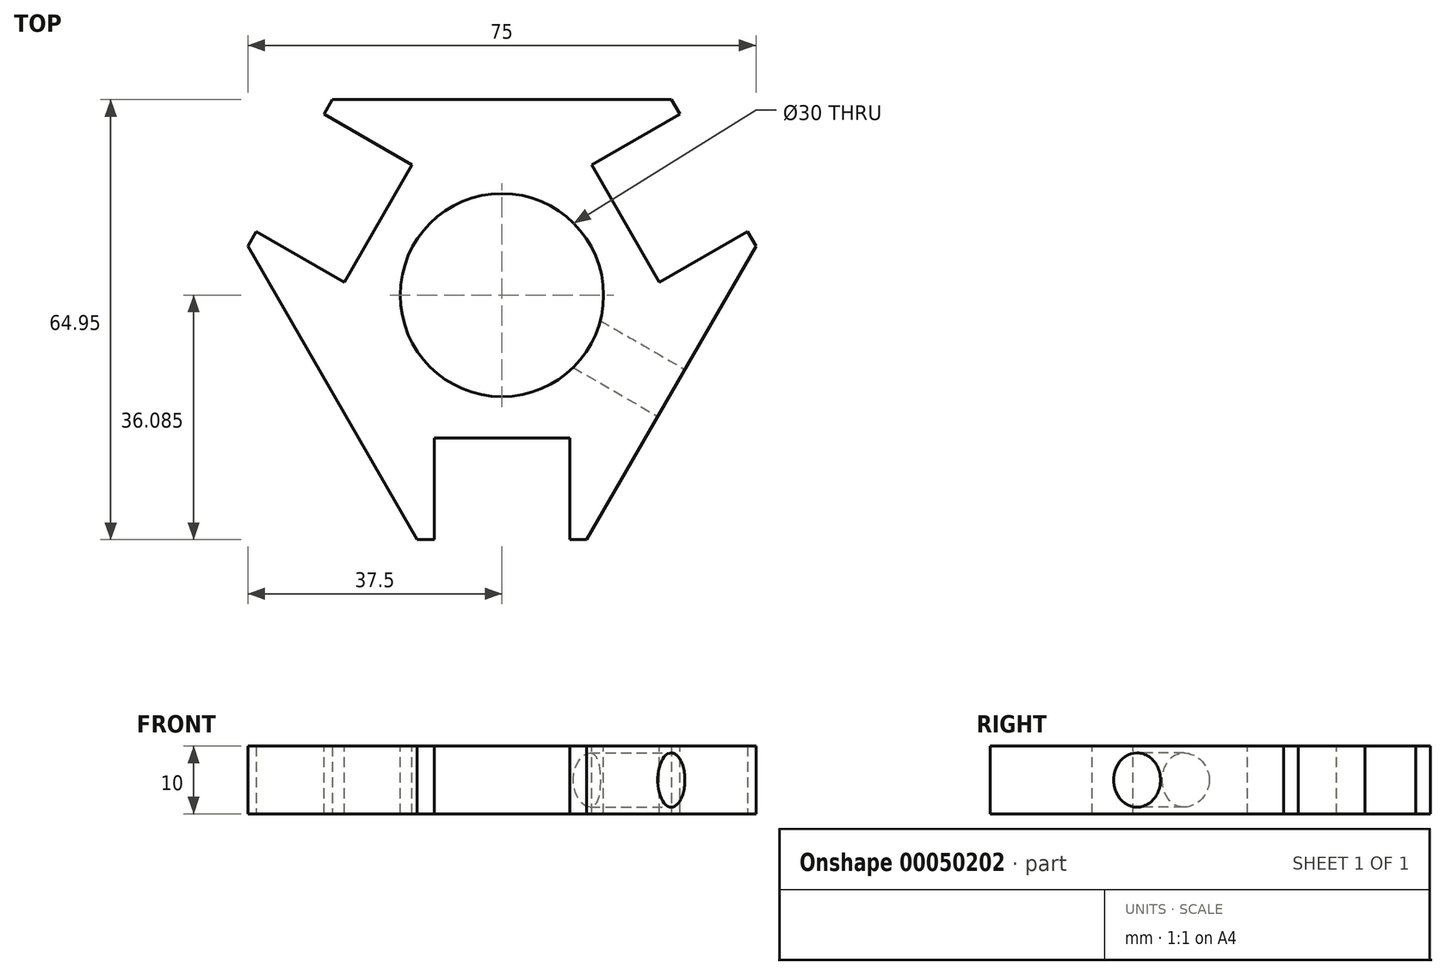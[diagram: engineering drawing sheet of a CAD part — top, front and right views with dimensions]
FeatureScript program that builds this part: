
annotation { "Feature Type Name" : "Feature", "Feature Type Description" : "" }
export const myFeature = defineFeature(function(context is Context, id is Id, definition is map)
    precondition{}
    {
        {
            var Q0;
            Q0=qCreatedBy(makeId("Top.planeOp"),FACE);
            var sketch = newSketch(context, id + "F0", { "sketchPlane" : qUnion([Q0])});
            skLineSegment(sketch, "E0", {"start": v(-50, 86.6) * mm, "end": v(50, 86.6) * mm});
            skLineSegment(sketch, "E1", {"start": v(50, 86.6) * mm, "end": v(0, 0) * mm});
            skLineSegment(sketch, "E2", {"start": v(0, 0) * mm, "end": v(-50, 86.6) * mm});
            skLineSegment(sketch, "E3", {"start": v(-25, 86.6) * mm, "end": v(-37.5, 64.95) * mm});
            skLineSegment(sketch, "E4", {"start": v(25, 86.6) * mm, "end": v(37.5, 64.95) * mm});
            skLineSegment(sketch, "E5", {"start": v(-12.5, 21.65) * mm, "end": v(12.5, 21.65) * mm});
            skSolve(sketch);
        }
        {
            var Q0;
            {var subQ0=sQuery(id+"F0.wireOp",EDGE,"E3");Q0=makeQuery(id+"F0.imprint","IMPRINT",FACE,{"disambiguationData":[TD([[makeQuery(id+"F0.imprint","IMPRINT",EDGE,{"derivedFrom":subQ0}),1.0]])]});}
            extrude(context, id + "F1", {"entities" : qUnion([Q0]), "depth" : 10 * mm});
        }
        {
            var Q0;
            Q0=makeQuery(id+"F1.opExtrude","CAP_FACE",FACE,{"disambiguationData":[OSD([sQuery(id+"F0.wireOp",EDGE,"E0"),sQuery(id+"F0.wireOp",EDGE,"E1"),sQuery(id+"F0.wireOp",EDGE,"E2"),sQuery(id+"F0.wireOp",EDGE,"E3"),sQuery(id+"F0.wireOp",EDGE,"E4"),sQuery(id+"F0.wireOp",EDGE,"E5")])],"isStart":false});
            var sketch = newSketch(context, id + "F2", { "sketchPlane" : qUnion([Q0])});
            skLineSegment(sketch, "E6.rect.bottom", {"start": v(-10, 36.65) * mm, "end": v(10, 36.65) * mm});
            skLineSegment(sketch, "E6.rect.top", {"start": v(-10, 6.65) * mm, "end": v(10, 6.65) * mm});
            skLineSegment(sketch, "E6.rect.left", {"start": v(-10, 36.65) * mm, "end": v(-10, 6.65) * mm});
            skLineSegment(sketch, "E6.rect.right", {"start": v(10, 36.65) * mm, "end": v(10, 6.65) * mm});
            skPoint(sketch, "E6.rect.middle", {"position": v(0, 21.65) * mm});
            skLineSegment(sketch, "E7", {"start": v(-23.26, 59.62) * mm, "end": v(-13.26, 76.94) * mm});
            skLineSegment(sketch, "E8", {"start": v(-13.26, 76.94) * mm, "end": v(-39.24, 91.94) * mm});
            skLineSegment(sketch, "E9", {"start": v(-39.24, 91.94) * mm, "end": v(-49.24, 74.62) * mm});
            skLineSegment(sketch, "E10", {"start": v(-49.24, 74.62) * mm, "end": v(-23.26, 59.62) * mm});
            skLineSegment(sketch, "E11", {"start": v(13.26, 76.94) * mm, "end": v(23.26, 59.62) * mm});
            skLineSegment(sketch, "E12", {"start": v(23.26, 59.62) * mm, "end": v(49.24, 74.62) * mm});
            skLineSegment(sketch, "E13", {"start": v(49.24, 74.62) * mm, "end": v(39.24, 91.94) * mm});
            skLineSegment(sketch, "E14", {"start": v(39.24, 91.94) * mm, "end": v(13.26, 76.94) * mm});
            skLineSegment(sketch, "E15", {"start": v(-39.24, 91.94) * mm, "end": v(-23.26, 59.62) * mm, "construction": true});
            skLineSegment(sketch, "E16", {"start": v(13.26, 76.94) * mm, "end": v(49.24, 74.62) * mm, "construction": true});
            skPoint(sketch, "E17", {"position": v(31.25, 75.78) * mm});
            skPoint(sketch, "E18", {"position": v(-31.25, 75.78) * mm});
            skLineSegment(sketch, "E19", {"start": v(-31.25, 75.78) * mm, "end": v(5.29, 54.68) * mm, "construction": true});
            skLineSegment(sketch, "E20", {"start": v(0, 86.6) * mm, "end": v(0, 51.6) * mm, "construction": true});
            skCircle(sketch, "E21", {"center": v(0, 57.74) * mm, "radius": 15 * mm});
            skSolve(sketch);
        }
        {
            var Q0;
            Q0 = qSketchRegion(id + "F2", true);
            extrude(context, id + "F3", {"entities" : qUnion([Q0]), "operationType" : NewBodyOperationType.REMOVE, "endBound" : BoundingType.THROUGH_ALL, "oppositeDirection" : true, "depth" : 25 * mm});
        }
        {
            var Q0;
            Q0=makeQuery(id+"F1.opExtrude","SWEPT_FACE",FACE,{"disambiguationData":[OSD([sQuery(id+"F0.wireOp",EDGE,"E1")])]});
            var sketch = newSketch(context, id + "F4", { "sketchPlane" : qUnion([Q0])});
            skCircle(sketch, "E22", {"center": v(50, 5) * mm, "radius": 4 * mm});
            skPoint(sketch, "E22.centerSnap0", {"position": v(25, 5) * mm});
            skPoint(sketch, "E22.centerSnap1", {"position": v(50, 10) * mm});
            skSolve(sketch);
        }
        {
            var Q0;
            Q0=makeQuery(id+"F4.imprint","IMPRINT",FACE,{"disambiguationData":[TD([[makeQuery(id+"F4.imprint","IMPRINT",EDGE,{"derivedFrom":sQuery(id+"F4.wireOp",EDGE,"E22")}),1.0]])]});
            var Q1;
            Q1=makeQuery(id+"F3.boolean.opBoolean","COPY",FACE,{"derivedFrom":makeQuery(id+"F3.opExtrude","SWEPT_FACE",FACE,{"disambiguationData":[OSD([sQuery(id+"F2.wireOp",EDGE,"E21")])]})});
            extrude(context, id + "F5", {"entities" : qUnion([Q0]), "operationType" : NewBodyOperationType.REMOVE, "endBound" : BoundingType.UP_TO_SURFACE, "oppositeDirection" : true, "endBoundEntityFace" : qUnion([Q1]), "depth" : 25 * mm});
        }
    });
